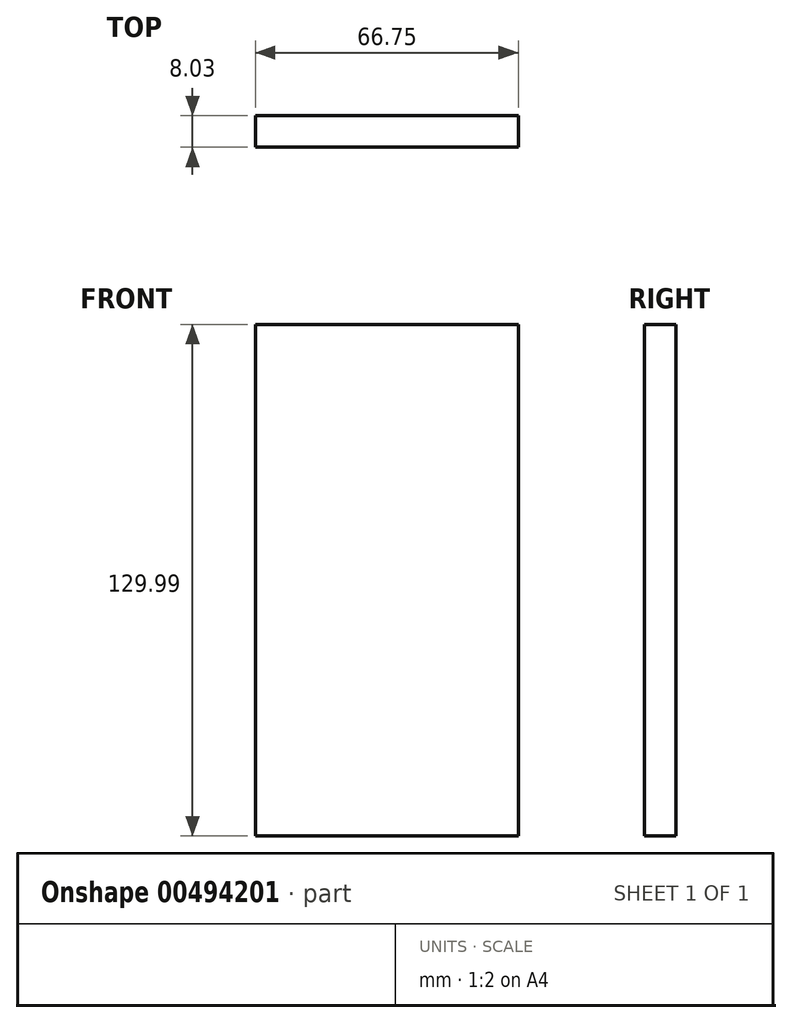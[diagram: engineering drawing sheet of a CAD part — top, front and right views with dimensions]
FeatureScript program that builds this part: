
annotation { "Feature Type Name" : "Feature", "Feature Type Description" : "" }
export const myFeature = defineFeature(function(context is Context, id is Id, definition is map)
    precondition{}
    {
        {
            var Q0;
            Q0=qCreatedBy(makeId("Front.planeOp"),FACE);
            var sketch = newSketch(context, id + "F0", { "sketchPlane" : qUnion([Q0])});
            skLineSegment(sketch, "E0.bottom", {"start": v(-30.9, 57.27) * mm, "end": v(35.85, 57.27) * mm});
            skLineSegment(sketch, "E0.top", {"start": v(-30.9, -72.72) * mm, "end": v(35.85, -72.72) * mm});
            skLineSegment(sketch, "E0.left", {"start": v(-30.9, 57.27) * mm, "end": v(-30.9, -72.72) * mm});
            skLineSegment(sketch, "E0.right", {"start": v(35.85, 57.27) * mm, "end": v(35.85, -72.72) * mm});
            skSolve(sketch);
        }
        {
            var Q0;
            Q0=makeQuery(id+"F0.imprint","IMPRINT",FACE,{"disambiguationData":[TD([[makeQuery(id+"F0.imprint","IMPRINT",EDGE,{"derivedFrom":sQuery(id+"F0.wireOp",EDGE,"E0.bottom")}),-1.0]])]});
            extrude(context, id + "F1", {"entities" : qUnion([Q0]), "depth" : 8.03 * mm});
        }
    });
